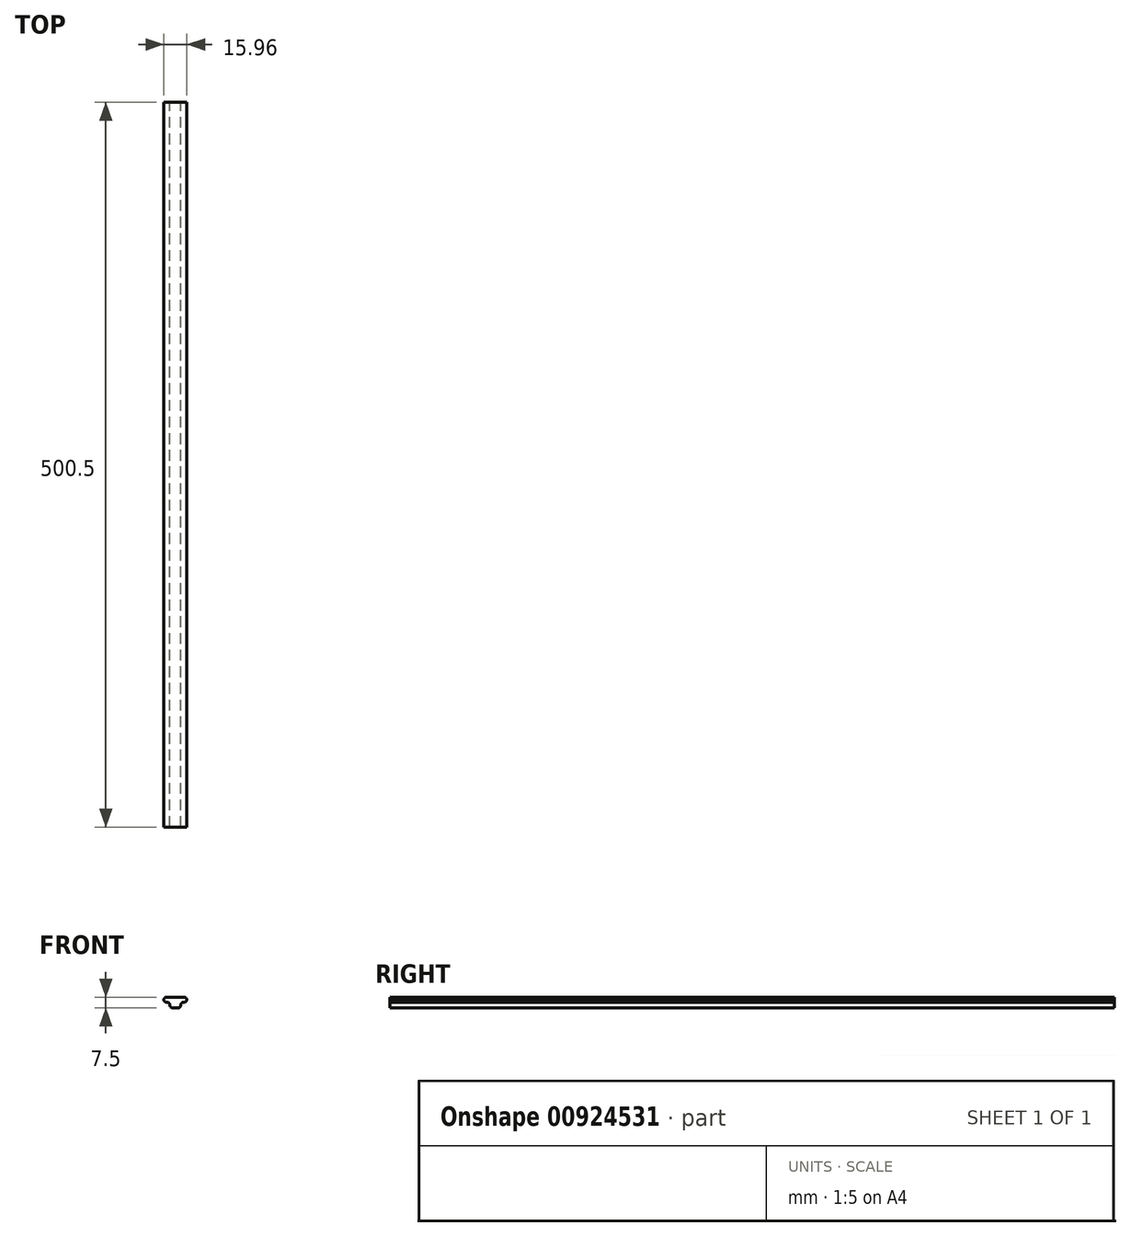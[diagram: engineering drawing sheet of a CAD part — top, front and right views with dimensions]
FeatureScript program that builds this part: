
annotation { "Feature Type Name" : "Feature", "Feature Type Description" : "" }
export const myFeature = defineFeature(function(context is Context, id is Id, definition is map)
    precondition{}
    {
        {
            var Q0;
            Q0=qCreatedBy(makeId("Front.planeOp"),FACE);
            var sketch = newSketch(context, id + "F0", { "sketchPlane" : qUnion([Q0])});
            skLineSegment(sketch, "E0", {"start": v(0, 0) * mm, "end": v(8, 0) * mm});
            skLineSegment(sketch, "E1.MirrorCS", {"start": v(0, 0) * mm, "end": v(-8, 0) * mm});
            skLineSegment(sketch, "E2", {"start": v(8, 0) * mm, "end": v(8, -3.5) * mm});
            skLineSegment(sketch, "E3.MirrorCS", {"start": v(-8, 0) * mm, "end": v(-8, -3.5) * mm});
            skLineSegment(sketch, "E4", {"start": v(-8, -3.5) * mm, "end": v(-3.75, -3.5) * mm});
            skLineSegment(sketch, "E5.MirrorCS", {"start": v(8, -3.5) * mm, "end": v(3.75, -3.5) * mm});
            skLineSegment(sketch, "E6", {"start": v(-3.75, -3.5) * mm, "end": v(-3.75, -7.5) * mm});
            skLineSegment(sketch, "E7.MirrorCS", {"start": v(3.75, -3.5) * mm, "end": v(3.75, -7.5) * mm});
            skLineSegment(sketch, "E8", {"start": v(-3.75, -7.5) * mm, "end": v(3.75, -7.5) * mm});
            skSolve(sketch);
        }
        {
            var Q0;
            Q0=makeQuery(id+"F0.imprint","IMPRINT",FACE,{"disambiguationData":[TD([[makeQuery(id+"F0.imprint","IMPRINT",EDGE,{"derivedFrom":sQuery(id+"F0.wireOp",EDGE,"E0")}),-1.0]])]});
            extrude(context, id + "F1", {"entities" : qUnion([Q0]), "depth" : 500.5 * mm, "offsetDistance" : 25 * mm});
        }
        {
            var Q0;
            Q0=makeQuery(id+"F1.opExtrude","SWEPT_EDGE",EDGE,{"disambiguationData":[OSD([sQuery(id+"F0.wireOp",EDGE,"E5.MirrorCS"),sQuery(id+"F0.wireOp",EDGE,"E7.MirrorCS")])]});
            var Q1;
            Q1=makeQuery(id+"F1.opExtrude","SWEPT_EDGE",EDGE,{"disambiguationData":[OSD([sQuery(id+"F0.wireOp",EDGE,"E7.MirrorCS"),sQuery(id+"F0.wireOp",EDGE,"E8")])]});
            var Q2;
            Q2=makeQuery(id+"F1.opExtrude","SWEPT_EDGE",EDGE,{"disambiguationData":[OSD([sQuery(id+"F0.wireOp",EDGE,"E6"),sQuery(id+"F0.wireOp",EDGE,"E8")])]});
            var Q3;
            Q3=makeQuery(id+"F1.opExtrude","SWEPT_EDGE",EDGE,{"disambiguationData":[OSD([sQuery(id+"F0.wireOp",EDGE,"E4"),sQuery(id+"F0.wireOp",EDGE,"E6")])]});
            var Q4;
            Q4=makeQuery(id+"F1.opExtrude","SWEPT_EDGE",EDGE,{"disambiguationData":[OSD([sQuery(id+"F0.wireOp",EDGE,"E3.MirrorCS"),sQuery(id+"F0.wireOp",EDGE,"E4")])]});
            var Q5;
            Q5=makeQuery(id+"F1.opExtrude","SWEPT_EDGE",EDGE,{"disambiguationData":[OSD([sQuery(id+"F0.wireOp",EDGE,"E1.MirrorCS"),sQuery(id+"F0.wireOp",EDGE,"E3.MirrorCS")])]});
            var Q6;
            Q6=makeQuery(id+"F1.opExtrude","SWEPT_EDGE",EDGE,{"disambiguationData":[OSD([sQuery(id+"F0.wireOp",EDGE,"E2"),sQuery(id+"F0.wireOp",EDGE,"E5.MirrorCS")])]});
            var Q7;
            Q7=makeQuery(id+"F1.opExtrude","SWEPT_EDGE",EDGE,{"disambiguationData":[OSD([sQuery(id+"F0.wireOp",EDGE,"E0"),sQuery(id+"F0.wireOp",EDGE,"E2")])]});
            fillet(context, id + "F2", {"entities" : qUnion([Q0, Q1, Q2, Q3, Q4, Q5, Q6, Q7]), "radius" : 2 * mm, "tangentPropagation" : true, "allowEdgeOverflow" : false});
        }
    });
